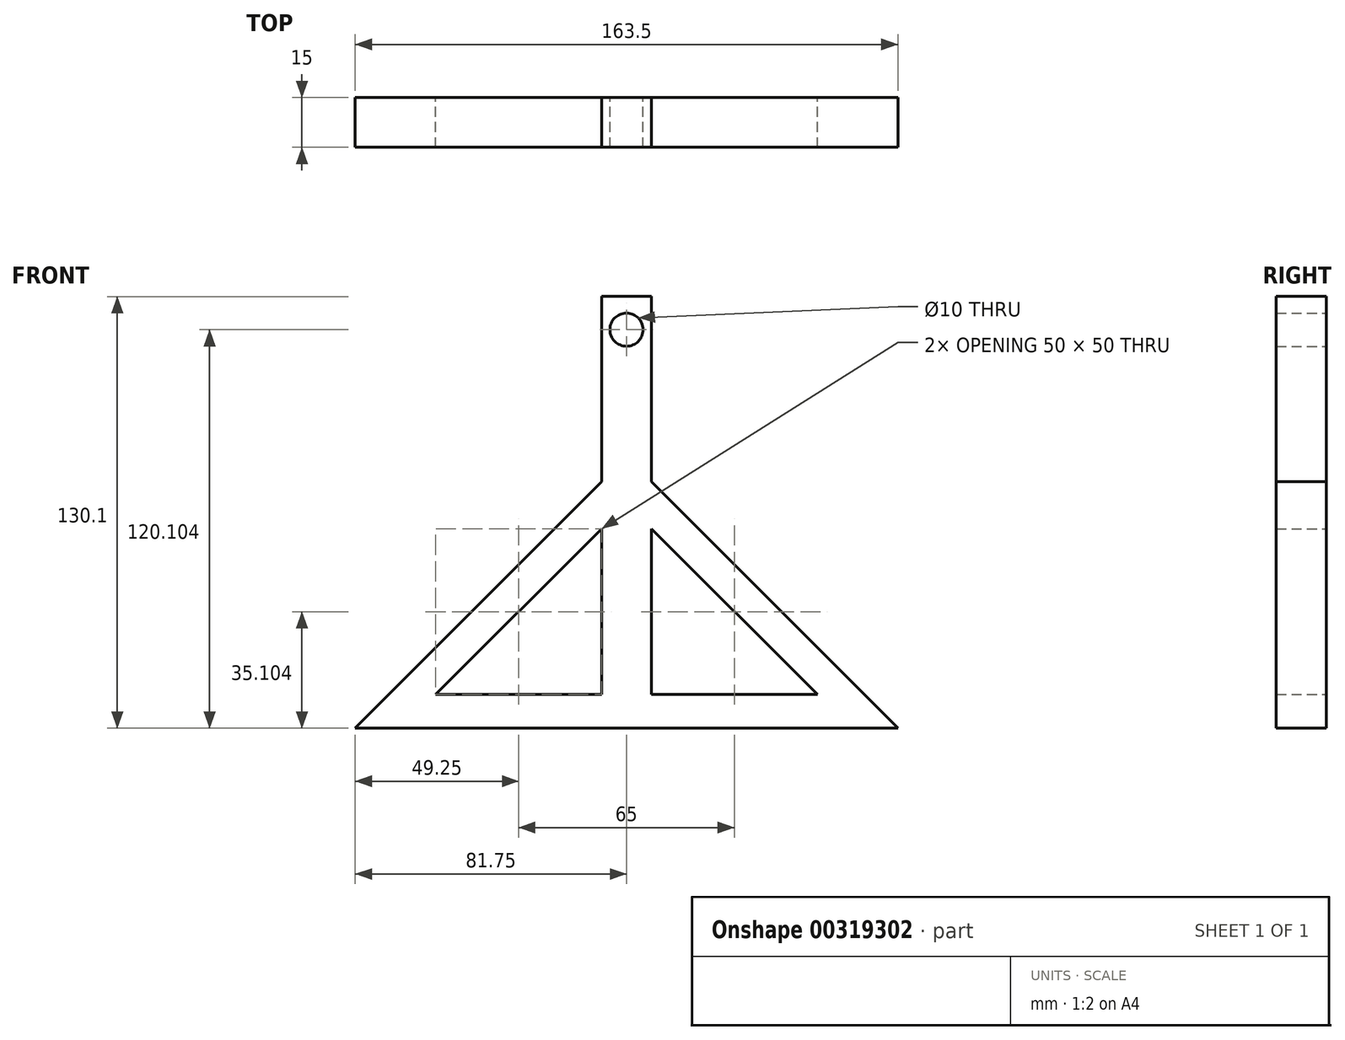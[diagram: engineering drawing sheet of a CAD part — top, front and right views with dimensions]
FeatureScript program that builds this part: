
annotation { "Feature Type Name" : "Feature", "Feature Type Description" : "" }
export const myFeature = defineFeature(function(context is Context, id is Id, definition is map)
    precondition{}
    {
        {
            var Q0;
            Q0=qCreatedBy(makeId("Front.planeOp"),FACE);
            var sketch = newSketch(context, id + "F0", { "sketchPlane" : qUnion([Q0])});
            skLineSegment(sketch, "E0", {"start": v(0, 74.25) * mm, "end": v(-74.25, 0) * mm});
            skLineSegment(sketch, "E1", {"start": v(-74.25, 0) * mm, "end": v(-60.1, 0) * mm});
            skLineSegment(sketch, "E2", {"start": v(-60.1, 0) * mm, "end": v(0, 60.1) * mm});
            skLineSegment(sketch, "E3", {"start": v(0, 60.1) * mm, "end": v(0, 74.25) * mm});
            skLineSegment(sketch, "E4", {"start": v(75.1, 0) * mm, "end": v(15, 60.1) * mm});
            skLineSegment(sketch, "E5", {"start": v(15, 60.1) * mm, "end": v(15, 74.25) * mm});
            skLineSegment(sketch, "E6", {"start": v(15, 74.25) * mm, "end": v(89.25, 0) * mm});
            skLineSegment(sketch, "E7", {"start": v(89.25, 0) * mm, "end": v(75.1, 0) * mm});
            skLineSegment(sketch, "E8", {"start": v(-50, 10.1) * mm, "end": v(65, 10.1) * mm});
            skLineSegment(sketch, "E9", {"start": v(75.1, 0) * mm, "end": v(-60.1, 0) * mm});
            skLineSegment(sketch, "E10", {"start": v(0, 10.1) * mm, "end": v(0, 130.1) * mm});
            skLineSegment(sketch, "E11", {"start": v(0, 130.1) * mm, "end": v(15, 130.1) * mm});
            skLineSegment(sketch, "E12", {"start": v(15, 130.1) * mm, "end": v(15, 10.1) * mm});
            skCircle(sketch, "E13", {"center": v(7.5, 120.1) * mm, "radius": 5 * mm});
            skSolve(sketch);
        }
        {
            var Q0;
            Q0 = qSketchRegion(id + "F0", true);
            extrude(context, id + "F1", {"entities" : qUnion([Q0]), "depth" : 15 * mm});
        }
    });
